# Revit family: Gleitlager T HV2, m.D., Ø64 bis Ø219mm (h=126mm bis 152mm)
name_source: partatom
category: HLS-Bauteile
revit_build: Autodesk Revit 2018 (Build: 20190510_1515(x64)
units: mm (PartAtom-declared; Revit-internal decimal feet)

## family parameters
Arbeitsebenenbasiert = Ja
Beim Laden mit Abzugskörper schneiden = Nein
Bemaßung runder Anschluss = Durchmesser verwenden
Gemeinsam genutzt = Ja
Immer vertikal = Nein
Klassifizierung = Keine
Raumberechnungspunkt = Nein
Teiletyp = Normal

## types (13) — shared parameters
Anzahl Rohrschellen = 2
Baustoffklasse = B2
Breite Schellenband = 50 mm
Breite Unterbau = 100 mm
Dämmstärke = 6 mm  [stored 0.019685 ft]
Fabrikat = MEFA
Hersteller = MEFA
Kurztext1 = Gleitlager T 2 RS HV2 50x5
Länge Unterbau = 250 mm
Mengeneinheit = St
Schalldämmeinlage = Gummi EPDM
Sicherheitsfaktor = 1.54
Stärke Material = 8 mm  [stored 0.0262467 ft]
Stärke Schellenband = 5 mm
Verschluss = Mutter / Verschluss-Schraube
Vorgabe-Ansicht = 1219 mm
max. Höhe Unterbau = 150 mm
max. Temperaturbeständigkeit = 100 °C
min. Höhe Unterbau = 125 mm
vpe = 1
zero-valued in all types: max. Rohraußendurchmesser, min. Rohraußendurchmesser

## per-type parameters (varying)
| type | Artikelnummer | EAN | Gewicht | Gewicht pro Bauteil | Kurztext2 | Schellenteil | max. Rohrachse | min. Rohrachse |
| Typ HV2, m. 2 RS, m.D., Ø64mm (h=126 bis 152mm) | 141bfbb0064 | 4250928461223 | 5.35 kg | 5.35 kg | 64 mm EPDM 100x250 mm fsv | TL-141S_b0076 bis 0231, m.D : mit RS Ø64mm m.D | 184 mm | 158 mm |
| Typ HV2, m. 2 RS, m.D., Ø76mm (h=126 bis 152mm) | 141bfbb0076 | 4250928461230 | 5.56 kg | 5.56 kg | 76 mm EPDM 100x250 mm fsv | TL-141S_b0076 bis 0231, m.D : mit RS Ø76mm m.D | 190 mm | 164 mm |
| Typ HV2, m. 2 RS, m.D., Ø89mm (h=126 bis 152mm) | 141bfbb0089 | 4250928461247 | 5.76 kg | 5.76 kg | 89 mm EPDM 100x250 mm fsv | TL-141S_b0076 bis 0231, m.D : mit RS Ø88.9mm, m.D | 197 mm | 171 mm |
| Typ HV2, m. 2 RS, m.D., Ø108mm (h=126 bis 152mm) | 141bfbb0108 | 4250928461254 | 6.06 kg | 6.06 kg | 108 mm EPDM 100x250 mm fsv | TL-141S_b0076 bis 0231, m.D : mit RS Ø108mm m.D | 206 mm | 180 mm |
| Typ HV2, m. 2 RS, m.D., Ø110mm (h=126 bis 152mm) | 141bfbb0110 | 4250928461261 | 6.10 kg | 6.10 kg | 110 mm EPDM 100x250 mm fsv | TL-141S_b0076 bis 0231, m.D : mit RS Ø110mm m.D | 207 mm | 181 mm |
| Typ HV2, m. 2 RS, m.D., Ø114mm (h=126 bis 152mm) | 141bfbb0114 | 4250928461278 | 6.16 kg | 6.16 kg | 114 mm EPDM 100x250 mm fsv | TL-141S_b0076 bis 0231, m.D : mit RS Ø114.3mm m.D | 209 mm | 183 mm |
| Typ HV2, m. 2 RS, m.D., Ø133mm (h=126 bis 152mm) | 141bfbb0133 | 4250928461285 | 6.46 kg | 6.46 kg | 133 mm EPDM 100x250 mm fsv | TL-141S_b0076 bis 0231, m.D : mit RS Ø133mm m.D | 219 mm | 193 mm |
| Typ HV2, m. 2 RS, m.D., Ø140mm (h=126 bis 152mm) | 141bfbb0140 | 4250928461292 | 6.58 kg | 6.58 kg | 140 mm EPDM 100x250 mm fsv | TL-141S_b0076 bis 0231, m.D : mit RS Ø139.7mm m.D | 222 mm | 196 mm |
| Typ HV2, m. 2 RS, m.D., Ø160mm (h=126 bis 152mm) | 141bfbb0160 | 4250928461308 | 6.90 kg | 6.90 kg | 160 mm EPDM 100x250 mm fsv | TL-141S_b0076 bis 0231, m.D : mit RS Ø160mm m.D | 232 mm | 206 mm |
| Typ HV2, m. 2 RS, m.D., Ø168mm (h=126 bis 152mm) | 141bfbb0168 | 4250928461315 | 7.03 kg | 7.03 kg | 168 mm EPDM 100x250 mm fsv | TL-141S_b0076 bis 0231, m.D : mit RS Ø168.3mm m.D | 236 mm | 210 mm |
| Typ HV2, m. 2 RS, m.D., Ø180mm (h=126 bis 152mm) | 141bfbb0180 | 4250928461322 | 7.22 kg | 7.22 kg | 180 mm EPDM 100x250 mm fsv | TL-141S_b0076 bis 0231, m.D : mit RS Ø180mm m.D | 242 mm | 216 mm |
| Typ HV2, m. 2 RS, m.D., Ø210mm (h=126 bis 152mm) | 141bfbb0210 | 4250928461339 | 7.70 kg | 7.70 kg | 210 mm EPDM 100x250 mm fsv | TL-141S_b0076 bis 0231, m.D : mit RS Ø210mm m.D | 257 mm | 231 mm |
| Typ HV2, m. 2 RS, m.D., Ø219mm (h=126 bis 152mm) | 141bfbb0219 | 4250928461346 | 7.84 kg | 7.84 kg | 219 mm EPDM 100x250 mm fsv | TL-141S_b0076 bis 0231, m.D : mit RS Ø219mm m.D | 262 mm | 236 mm |

note: [stored X ft] marks values corroborated as IEEE doubles in the binary element streams (Revit-internal decimal feet)

## geometry (parser evidence)
native form markers: Sweep x10
no freeform markers — native parametric forms only
